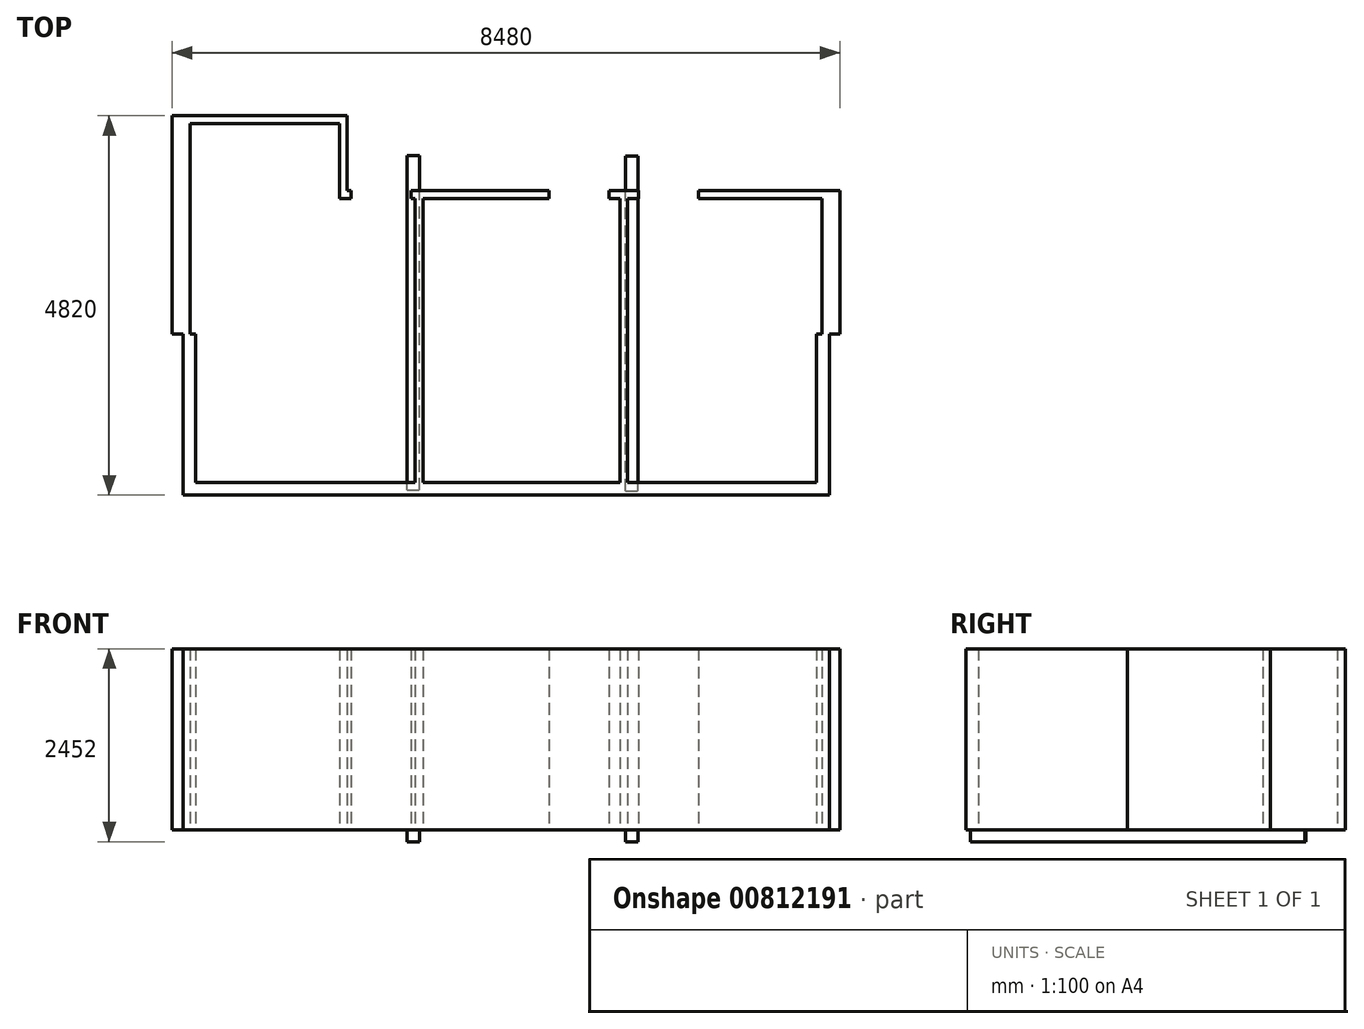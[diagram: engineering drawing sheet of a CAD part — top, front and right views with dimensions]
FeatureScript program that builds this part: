
annotation { "Feature Type Name" : "Feature", "Feature Type Description" : "" }
export const myFeature = defineFeature(function(context is Context, id is Id, definition is map)
    precondition{}
    {
        {
            var Q0;
            Q0=qCreatedBy(makeId("Top.planeOp"),FACE);
            var sketch = newSketch(context, id + "F0", { "sketchPlane" : qUnion([Q0])});
            skLineSegment(sketch, "E0", {"start": v(0, -1222.53) * mm, "end": v(2790, -1222.53) * mm});
            skLineSegment(sketch, "E1", {"start": v(-160, 666.86) * mm, "end": v(-295, 666.86) * mm});
            skLineSegment(sketch, "E2", {"start": v(8050, -1382.53) * mm, "end": v(8050, 666.86) * mm});
            skLineSegment(sketch, "E3", {"start": v(7960, 666.86) * mm, "end": v(7890, 666.86) * mm});
            skLineSegment(sketch, "E4", {"start": v(7960, 2387.47) * mm, "end": v(7960, 666.86) * mm});
            skLineSegment(sketch, "E5", {"start": v(8185, 666.86) * mm, "end": v(8185, 2387.47) * mm});
            skLineSegment(sketch, "E6", {"start": v(7890, 666.86) * mm, "end": v(7890, -1222.53) * mm});
            skLineSegment(sketch, "E7", {"start": v(-160, 666.86) * mm, "end": v(-160, -1382.53) * mm});
            skLineSegment(sketch, "E8", {"start": v(0, 666.86) * mm, "end": v(0, -1222.53) * mm});
            skLineSegment(sketch, "E9", {"start": v(8050, -1382.53) * mm, "end": v(-160, -1382.53) * mm});
            skLineSegment(sketch, "E10", {"start": v(5490, 2387.47) * mm, "end": v(5490, -1222.53) * mm});
            skLineSegment(sketch, "E11", {"start": v(5390, 2387.47) * mm, "end": v(5390, -1222.53) * mm});
            skLineSegment(sketch, "E12", {"start": v(7960, 2487.47) * mm, "end": v(1928, 2487.47) * mm});
            skLineSegment(sketch, "E13", {"start": v(7960, 2387.47) * mm, "end": v(5490, 2387.47) * mm});
            skLineSegment(sketch, "E14", {"start": v(5390, 2387.47) * mm, "end": v(2890, 2387.47) * mm});
            skLineSegment(sketch, "E15", {"start": v(1828, 2387.47) * mm, "end": v(1828, 3337.47) * mm});
            skLineSegment(sketch, "E16", {"start": v(1928, 2487.47) * mm, "end": v(1928, 3437.47) * mm});
            skLineSegment(sketch, "E17", {"start": v(1928, 3437.47) * mm, "end": v(-295, 3437.47) * mm});
            skLineSegment(sketch, "E18", {"start": v(2890, 2387.47) * mm, "end": v(2890, -1222.53) * mm});
            skLineSegment(sketch, "E19", {"start": v(2790, 2387.47) * mm, "end": v(2790, -1222.53) * mm});
            skLineSegment(sketch, "E20", {"start": v(5252, 2487.47) * mm, "end": v(5252, 2387.47) * mm});
            skLineSegment(sketch, "E21", {"start": v(4490, 2487.47) * mm, "end": v(4490, 2387.47) * mm});
            skLineSegment(sketch, "E22", {"start": v(1978, 2487.47) * mm, "end": v(1978, 2387.47) * mm});
            skLineSegment(sketch, "E23", {"start": v(2740, 2487.47) * mm, "end": v(2740, 2387.47) * mm});
            skLineSegment(sketch, "E24", {"start": v(1828, 3337.47) * mm, "end": v(-70, 3337.47) * mm});
            skPoint(sketch, "E24.endSnap0", {"position": v(-70, 666.86) * mm});
            skLineSegment(sketch, "E25", {"start": v(-70, 3337.47) * mm, "end": v(-70, 666.86) * mm});
            skLineSegment(sketch, "E26", {"start": v(-295, 3437.47) * mm, "end": v(-295, 666.86) * mm});
            skLineSegment(sketch, "E27", {"start": v(6392, 2487.47) * mm, "end": v(6392, 2387.47) * mm});
            skLineSegment(sketch, "E28", {"start": v(5630, 2487.47) * mm, "end": v(5630, 2387.47) * mm});
            skArc(sketch, "E29", {"start": v(6392, 2437.47) * mm, "mid": v(6168.82, 1898.65) * mm, "end": v(5630, 1675.47) * mm});
            skLineSegment(sketch, "E30", {"start": v(5630, 2437.47) * mm, "end": v(5630, 1675.47) * mm});
            skArc(sketch, "E31", {"start": v(4490, 2437.47) * mm, "mid": v(4713.18, 1898.65) * mm, "end": v(5252, 1675.47) * mm});
            skLineSegment(sketch, "E32", {"start": v(5252, 1675.47) * mm, "end": v(5252, 2437.47) * mm});
            skArc(sketch, "E33", {"start": v(1978, 2437.47) * mm, "mid": v(2201.18, 1898.65) * mm, "end": v(2740, 1675.47) * mm});
            skLineSegment(sketch, "E34", {"start": v(2740, 1675.47) * mm, "end": v(2740, 2437.47) * mm});
            skLineSegment(sketch, "E35.trimOffspring", {"start": v(2790, 2387.47) * mm, "end": v(1828, 2387.47) * mm});
            skLineSegment(sketch, "E36", {"start": v(-70, 666.86) * mm, "end": v(0, 666.86) * mm});
            skLineSegment(sketch, "E37", {"start": v(8050, 666.86) * mm, "end": v(8185, 666.86) * mm});
            skLineSegment(sketch, "E38.trimOffspring", {"start": v(2890, -1222.53) * mm, "end": v(5390, -1222.53) * mm});
            skLineSegment(sketch, "E39.trimOffspring", {"start": v(5490, -1222.53) * mm, "end": v(7890, -1222.53) * mm});
            skLineSegment(sketch, "E40", {"start": v(7960, 2487.47) * mm, "end": v(8185, 2487.47) * mm});
            skLineSegment(sketch, "E41", {"start": v(8185, 2487.47) * mm, "end": v(8185, 2387.47) * mm});
            skSolve(sketch);
        }
        {
            var Q0;
            Q0=makeQuery(id+"F0.imprint","IMPRINT",FACE,{"disambiguationData":[TD([[makeQuery(id+"F0.imprint","IMPRINT",EDGE,{"derivedFrom":sQuery(id+"F0.wireOp",EDGE,"E0")}),-1.0]])]});
            extrude(context, id + "F1", {"entities" : qUnion([Q0]), "depth" : 2300 * mm, "offsetDistance" : 25 * mm});
        }
        {
            var Q0;
            Q0=qCreatedBy(makeId("Top.planeOp"),FACE);
            var sketch = newSketch(context, id + "F2", { "sketchPlane" : qUnion([Q0])});
            skLineSegment(sketch, "E42.bottom", {"start": v(2690, -1315.16) * mm, "end": v(2845, -1315.16) * mm});
            skLineSegment(sketch, "E42.top", {"start": v(2690, 2934.84) * mm, "end": v(2845, 2934.84) * mm});
            skLineSegment(sketch, "E42.left", {"start": v(2690, -1315.16) * mm, "end": v(2690, 2934.84) * mm});
            skLineSegment(sketch, "E42.right", {"start": v(2845, -1315.16) * mm, "end": v(2845, 2934.84) * mm});
            skLineSegment(sketch, "E43.bottom", {"start": v(5465, -1325.86) * mm, "end": v(5620, -1325.86) * mm});
            skLineSegment(sketch, "E43.top", {"start": v(5465, 2924.14) * mm, "end": v(5620, 2924.14) * mm});
            skLineSegment(sketch, "E43.left", {"start": v(5465, -1325.86) * mm, "end": v(5465, 2924.14) * mm});
            skLineSegment(sketch, "E43.right", {"start": v(5620, -1325.86) * mm, "end": v(5620, 2924.14) * mm});
            skSolve(sketch);
        }
        {
            var Q0;
            Q0 = qSketchRegion(id + "F2", true);
            extrude(context, id + "F3", {"entities" : qUnion([Q0]), "operationType" : NewBodyOperationType.ADD, "depth" : -152 * mm, "offsetDistance" : 25 * mm});
        }
    });
